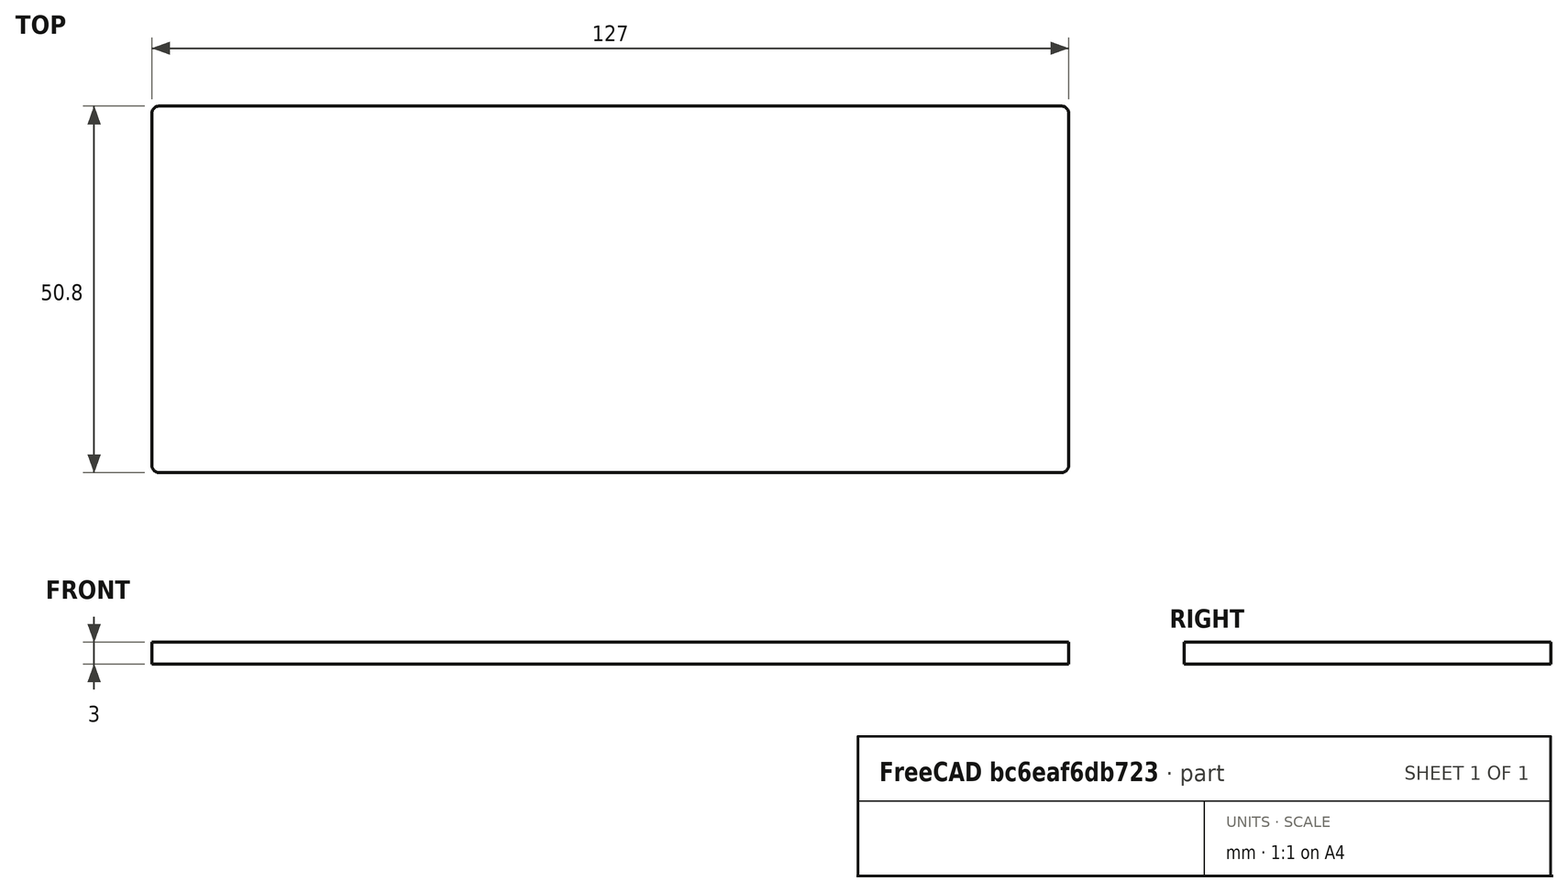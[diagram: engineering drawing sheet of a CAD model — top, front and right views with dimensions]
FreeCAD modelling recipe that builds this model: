
FCSTD DOCUMENT  (FreeCAD 0.20R29603 (Git))
Label: 5in_x_2in
License: All rights reserved
LicenseURL: http://en.wikipedia.org/wiki/All_rights_reserved
objects: Spreadsheet::Sheet×1, Sketcher::SketchObject×1, PartDesign::Pad×1, PartDesign::Body×1
note: 4 computed .brp shape members not serialized (recipe doc carries the construction recipe); baked Part::Feature solids carry a one-line shape summary decoded from their .brp

FEATURE [Spreadsheet::Sheet] Spreadsheet
  cells = A2=Length; B2(Length)==5in; A3=Width; B3(Width)==2in; A4=Thickness; B4(Thickness)==3mm; A5=FilletRadius; B5(FilletRadius)==1mm
FEATURE [Sketcher::SketchObject] Sketch
  FullyConstrained = true
  MapMode = 5
  Support = -> [XY_Plane]
  expr: Constraints[19] = Spreadsheet.FilletRadius
  expr: Constraints[21] = Spreadsheet.Length
  expr: Constraints[22] = Spreadsheet.Width
  sketch-geometry (10):
    g0: ArcOfCircle CenterX=-62.5 CenterY=24.4 CenterZ=0 NormalX=0 NormalY=0 NormalZ=1 AngleXU=0 Radius=1 StartAngle=1.5708 EndAngle=3.14159
    g1: LineSegment StartX=-62.5 StartY=25.4 StartZ=0 EndX=62.5 EndY=25.4 EndZ=0
    g2: ArcOfCircle CenterX=62.5 CenterY=24.4 CenterZ=0 NormalX=0 NormalY=0 NormalZ=1 AngleXU=0 Radius=1 StartAngle=2.6386e-12 EndAngle=1.5708
    g3: LineSegment StartX=63.5 StartY=24.4 StartZ=0 EndX=63.5 EndY=-24.4 EndZ=0
    g4: ArcOfCircle CenterX=62.5 CenterY=-24.4 CenterZ=0 NormalX=0 NormalY=0 NormalZ=1 AngleXU=0 Radius=1 StartAngle=4.71239 EndAngle=6.28319
    g5: LineSegment StartX=62.5 StartY=-25.4 StartZ=0 EndX=-62.5 EndY=-25.4 EndZ=0
    g6: ArcOfCircle CenterX=-62.5 CenterY=-24.4 CenterZ=0 NormalX=0 NormalY=0 NormalZ=1 AngleXU=0 Radius=1 StartAngle=3.14159 EndAngle=4.71239
    g7: LineSegment StartX=-63.5 StartY=-24.4 StartZ=0 EndX=-63.5 EndY=24.4 EndZ=0
    g8: GeomPoint X=-63.5 Y=25.4 Z=0
    g9: GeomPoint X=63.5 Y=-25.4 Z=0
  constraints (23):
    c: Tangent(g0,g1) = 1.5708
    c: Tangent(g1,g2) = 1.5708
    c: Tangent(g2,g3) = 1.5708
    c: Tangent(g3,g4) = 1.5708
    c: Tangent(g4,g5) = 1.5708
    c: Tangent(g5,g6) = 1.5708
    c: Tangent(g6,g7) = 1.5708
    c: Tangent(g7,g0) = 1.5708
    c: Horizontal(g1)
    c: Horizontal(g5)
    c: Vertical(g3)
    c: Vertical(g7)
    c: Equal(g0,g2)
    c: Equal(g2,g4)
    c: Equal(g4,g6)
    c: PointOnObject(g8,g1)
    c: PointOnObject(g8,g7)
    c: PointOnObject(g9,g3)
    c: PointOnObject(g9,g5)
    c: Radius(g4) = 1
    c: Symmetric(g8,g9,g-1)
    c: DistanceX(g6,g3) = 127
    c: DistanceY(g4,g1) = 50.8
FEATURE [PartDesign::Pad] Pad
  Direction = (0,0,1)
  Length = 3
  Length2 = 10
  Profile = -> Sketch
  ReferenceAxis = -> Sketch [N_Axis]
  Type = 0
  expr: Length = Spreadsheet.Thickness
FEATURE [PartDesign::Body] Body
  Group = -> [Sketch,Pad]
  Origin = -> Origin
  Tip = -> Pad
